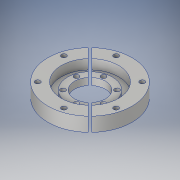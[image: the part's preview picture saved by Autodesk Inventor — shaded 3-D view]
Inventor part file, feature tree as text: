
AUTODESK INVENTOR PART (.ipt)
format: ipt  version: 2018 (Build 220112000, 112)  size: 189,952 bytes
history: native  units: in
note: dims shown in document units (in); Inventor stores cm internally (conversion verified against a paired STEP export)
features: sketch x6, extrude x4, hole x2, pattern_circular x2
ambient origin geometry x8: Origin, YZ Plane, XZ Plane, XY Plane, X Axis, Y Axis, Z Axis, Center Point
bodies: Solid1 (feature_tree)
feature tree (14):
  extrude  "Extrusion1"  Depth=3.0in
  extrude  "Extrusion2"  Depth=0.25in
  hole  "Hole1"  [1 undecoded]
  pattern_circular  "Circular Pattern1"  Count=6 Angle=360.0deg
  extrude  "Extrusion5"  Depth=0.25in TaperAngle=0.0deg
  hole  "Hole3"  [1 undecoded]
  pattern_circular  "Circular Pattern3"  Angle=45.0deg  [1 undecoded]
  extrude  "Extrusion6"  Depth=0.25in TaperAngle=360.0deg
  sketch  "Sketch1"  dims[d0=1.1in d1=3.0in]
  sketch  "Sketch2"  dims[d2=0.5in d3=0.0in d4=0.25in]
  sketch  "Sketch3"  dims[d5=0.35in d6=0.0in d7=0.68in]
  sketch  "Sketch8"  dims[d8=45.0deg]
  sketch  "Sketch9"  dims[d9=0.177in d10=0.75in d11=0.385in d12=0.25in d13=0.5635in d14=1.0in d15=0.8108in d19=2.3622in d20=360.0deg]
  sketch  "Sketch10"  dims[d41=0.22in d45=0.25in d46=0.0in d47=0.18in d48=45.0deg d49=0.177in d50=0.75in d51=0.332in d52=0.25in d53=0.5635in d54=1.0in d55=0.8108in d56=2.3622in d57=360.0deg d59=135.0deg d60=0.1in d61=0.25in d62=0.0in]
note: 3 required parameter values undecoded (feature->parameter linkage not recoverable at this tier; creation-order binding heuristic only, values carry confidence <= 0.55)
